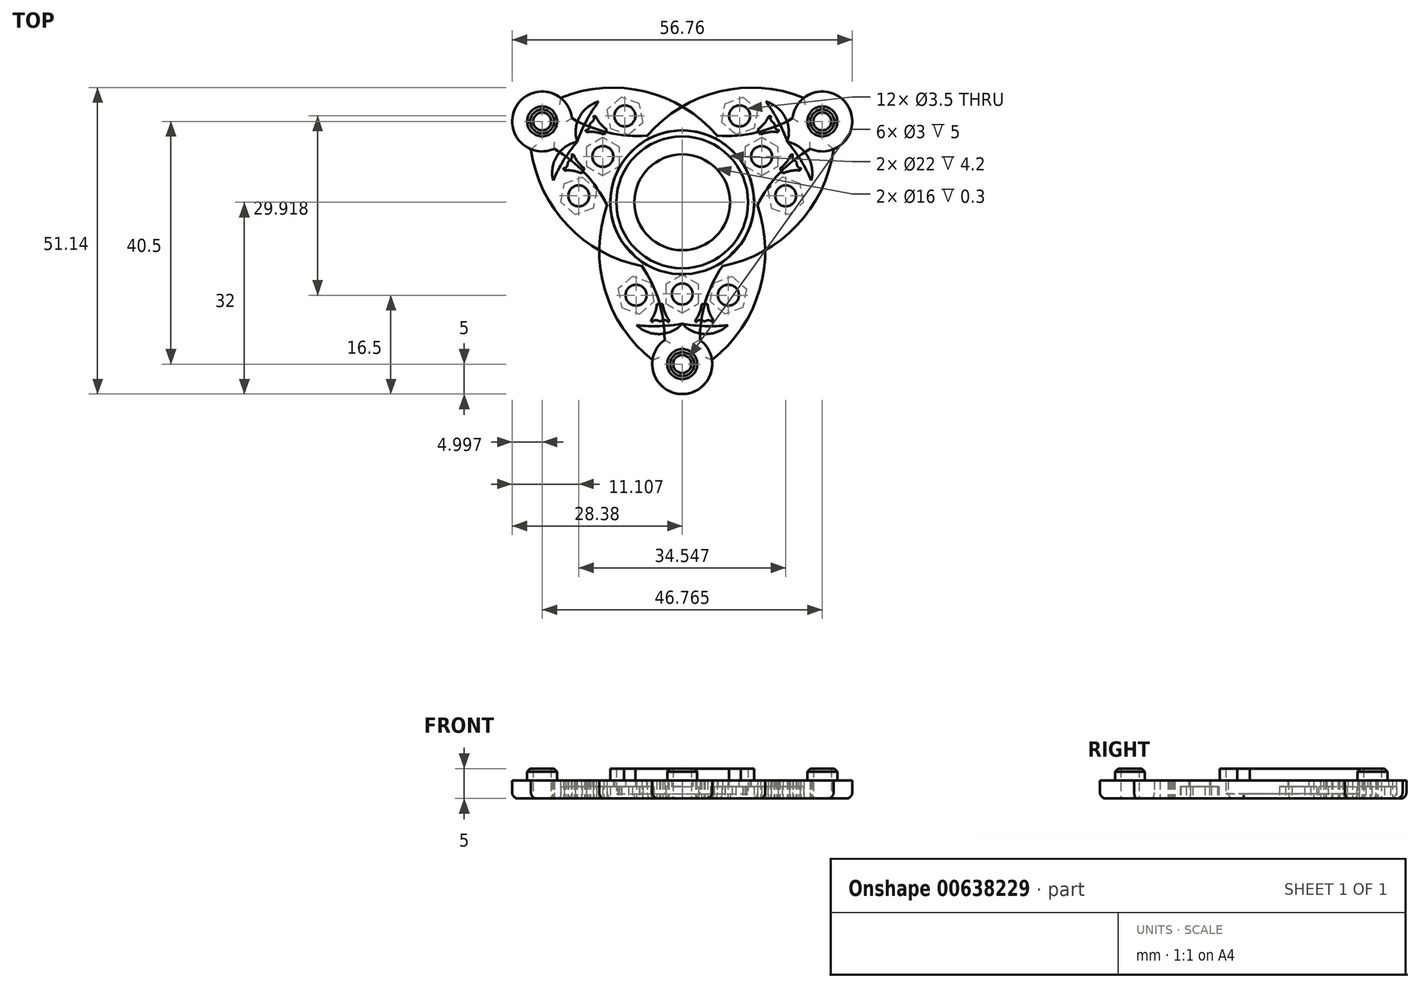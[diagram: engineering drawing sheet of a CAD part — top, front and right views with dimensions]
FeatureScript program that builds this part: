
annotation { "Feature Type Name" : "Feature", "Feature Type Description" : "" }
export const myFeature = defineFeature(function(context is Context, id is Id, definition is map)
    precondition{}
    {
        {
            var Q0;
            Q0=qCreatedBy(makeId("Top.planeOp"),FACE);
            var sketch = newSketch(context, id + "F0", { "sketchPlane" : qUnion([Q0])});
            skCircle(sketch, "E0", {"center": v(0, 0) * mm, "radius": 12 * mm});
            skArc(sketch, "E1", {"start": v(4, -27) * mm, "mid": v(12.97, -14.42) * mm, "end": v(11.96, 1) * mm});
            skCircle(sketch, "E2", {"center": v(0, -27) * mm, "radius": 4 * mm});
            skCircle(sketch, "E3", {"center": v(7.7, -15.5) * mm, "radius": 1.75 * mm});
            skArc(sketch, "E4", {"start": v(-3, -24.35) * mm, "mid": v(-4.45, -14.93) * mm, "end": v(-9.75, -7) * mm});
            skCircle(sketch, "E5.cCircle", {"center": v(7.7, -15.5) * mm, "radius": 2.75 * mm, "construction": true});
            skLineSegment(sketch, "E5.0", {"start": v(4.7, -16.54) * mm, "end": v(5.3, -13.42) * mm});
            skLineSegment(sketch, "E5.1", {"start": v(5.3, -13.42) * mm, "end": v(8.3, -12.38) * mm});
            skLineSegment(sketch, "E5.2", {"start": v(8.3, -12.38) * mm, "end": v(10.7, -14.46) * mm});
            skLineSegment(sketch, "E5.3", {"start": v(10.7, -14.46) * mm, "end": v(10.1, -17.58) * mm});
            skLineSegment(sketch, "E5.4", {"start": v(10.1, -17.58) * mm, "end": v(7.1, -18.62) * mm});
            skLineSegment(sketch, "E5.5", {"start": v(7.1, -18.62) * mm, "end": v(4.7, -16.54) * mm});
            skPoint(sketch, "E5.0.midPoint", {"position": v(5, -14.98) * mm});
            skCircle(sketch, "E6", {"center": v(0, -27) * mm, "radius": 5 * mm});
            skCircle(sketch, "E7.cCircle", {"center": v(0, -15.3) * mm, "radius": 2.75 * mm, "construction": true});
            skLineSegment(sketch, "E7.0", {"start": v(2.75, -13.71) * mm, "end": v(2.75, -16.89) * mm});
            skLineSegment(sketch, "E7.1", {"start": v(2.75, -16.89) * mm, "end": v(0, -18.48) * mm});
            skLineSegment(sketch, "E7.2", {"start": v(0, -18.48) * mm, "end": v(-2.75, -16.89) * mm});
            skLineSegment(sketch, "E7.3", {"start": v(-2.75, -16.89) * mm, "end": v(-2.75, -13.71) * mm});
            skLineSegment(sketch, "E7.4", {"start": v(-2.75, -13.71) * mm, "end": v(0, -12.12) * mm});
            skLineSegment(sketch, "E7.5", {"start": v(0, -12.12) * mm, "end": v(2.75, -13.71) * mm});
            skPoint(sketch, "E7.0.midPoint", {"position": v(2.75, -15.3) * mm});
            skCircle(sketch, "E8", {"center": v(0, -15.3) * mm, "radius": 1.75 * mm});
            skArc(sketch, "E9", {"start": v(0, -20.25) * mm, "mid": v(3.75, -21.98) * mm, "end": v(7.6, -20.5) * mm});
            skArc(sketch, "E10", {"start": v(0, -20.25) * mm, "mid": v(3.8, -20.65) * mm, "end": v(7.6, -20.5) * mm});
            skArc(sketch, "E11", {"start": v(4.9, -20) * mm, "mid": v(5.16, -19.81) * mm, "end": v(5.1, -19.5) * mm});
            skArc(sketch, "E12", {"start": v(3.6, -19.88) * mm, "mid": v(3, -19.66) * mm, "end": v(2.4, -19.88) * mm});
            skArc(sketch, "E13", {"start": v(2.3, -19.5) * mm, "mid": v(2.2, -19.78) * mm, "end": v(2.4, -20) * mm});
            skLineSegment(sketch, "E14", {"start": v(4.9, -20) * mm, "end": v(5, -19.92) * mm});
            skLineSegment(sketch, "E15", {"start": v(3.8, -19.88) * mm, "end": v(3.6, -19.88) * mm});
            skLineSegment(sketch, "E16", {"start": v(2.4, -19.88) * mm, "end": v(2.4, -20) * mm});
            skArc(sketch, "E17", {"start": v(4.25, -17) * mm, "mid": v(4.5, -18.3) * mm, "end": v(5.1, -19.5) * mm});
            skArc(sketch, "E18", {"start": v(5, -19.92) * mm, "mid": v(4.4, -19.68) * mm, "end": v(3.8, -19.88) * mm});
            skArc(sketch, "E19", {"start": v(2.3, -19.5) * mm, "mid": v(2.95, -18.31) * mm, "end": v(3.25, -17) * mm});
            skLineSegment(sketch, "E20", {"start": v(3.25, -17) * mm, "end": v(4.25, -17) * mm});
            skCircle(sketch, "E21", {"center": v(0, -27) * mm, "radius": 2.5 * mm});
            skCircle(sketch, "E22", {"center": v(0, -27) * mm, "radius": 1.5 * mm});
            skCircle(sketch, "E23", {"center": v(0, 0) * mm, "radius": 11 * mm});
            skCircle(sketch, "E24", {"center": v(0, 0) * mm, "radius": 8 * mm});
            skSolve(sketch);
        }
        {
            var Q0;
            {var subQ2=sQuery(id+"F0.wireOp",EDGE,"aa2ff135-aea7-4953-97f4-e412ee23423b.2.4");Q0=makeQuery(id+"F0.imprint","IMPRINT",FACE,{"disambiguationData":[TD([[makeQuery(id+"F0.imprint","IMPRINT",EDGE,{"derivedFrom":subQ2}),-1.0]])]});}
            var Q1;
            {var subQ8=sQuery(id+"F0.wireOp",EDGE,"aa2ff135-aea7-4953-97f4-e412ee23423b.1.4");Q1=makeQuery(id+"F0.imprint","IMPRINT",FACE,{"disambiguationData":[TD([[makeQuery(id+"F0.imprint","IMPRINT",EDGE,{"derivedFrom":subQ8}),-1.0]])]});}
            var Q2;
            {var subQ25=sQuery(id+"F0.wireOp",EDGE,"OuvVGkWf-tbSn-ko2d-VdRC-dNZ10hL7c7yv");Q2=makeQuery(id+"F0.imprint","IMPRINT",FACE,{"disambiguationData":[TD([[makeQuery(id+"F0.imprint","IMPRINT",EDGE,{"derivedFrom":subQ25}),-1.0]])]});}
            var Q3;
            {var subQ0=sQuery(id+"F0.wireOp",EDGE,"E1");var subQ1=sQuery(id+"F0.wireOp",EDGE,"E0");var subQ2=makeQuery(id+"F0.imprint","INTERSECT",VERTEX,{"derivedFrom":[subQ1,subQ0]});Q3=makeQuery(id+"F0.imprint","IMPRINT",FACE,{"disambiguationData":[TD([[makeQuery(id+"F0.imprint","IMPRINT",EDGE,{"disambiguationData":[TD([[subQ2,1.0]])],"derivedFrom":subQ1}),-1.0]])]});}
            var Q4;
            Q4=makeQuery(id+"F0.imprint","IMPRINT",FACE,{"disambiguationData":[TD([[makeQuery(id+"F0.imprint","IMPRINT",EDGE,{"derivedFrom":sQuery(id+"F0.wireOp",EDGE,"VsIOrWzV-Qm02-VE6o-2Dnz-qWALikvy4E2U")}),-1.0]])]});
            var Q5;
            {var subQ0=sQuery(id+"F0.wireOp",EDGE,"aa2ff135-aea7-4953-97f4-e412ee23423b.2.3");var subQ1=sQuery(id+"F0.wireOp",EDGE,"E0");var subQ2=makeQuery(id+"F0.imprint","INTERSECT",VERTEX,{"derivedFrom":[subQ1,subQ0]});Q5=makeQuery(id+"F0.imprint","IMPRINT",FACE,{"disambiguationData":[TD([[makeQuery(id+"F0.imprint","IMPRINT",EDGE,{"disambiguationData":[TD([[subQ2,1.0]])],"derivedFrom":subQ1}),-1.0]])]});}
            var Q6;
            {var subQ0=sQuery(id+"F0.wireOp",EDGE,"aa2ff135-aea7-4953-97f4-e412ee23423b.1.3");var subQ1=sQuery(id+"F0.wireOp",EDGE,"E0");var subQ2=makeQuery(id+"F0.imprint","INTERSECT",VERTEX,{"derivedFrom":[subQ1,subQ0]});Q6=makeQuery(id+"F0.imprint","IMPRINT",FACE,{"disambiguationData":[TD([[makeQuery(id+"F0.imprint","IMPRINT",EDGE,{"disambiguationData":[TD([[subQ2,1.0]])],"derivedFrom":subQ1}),-1.0]])]});}
            var Q7;
            {var subQ0=sQuery(id+"F0.wireOp",EDGE,"E2");var subQ1=sQuery(id+"F0.wireOp",EDGE,"E1");var subQ2=makeQuery(id+"F0.imprint","INTERSECT",VERTEX,{"derivedFrom":[subQ1,subQ0]});Q7=makeQuery(id+"F0.imprint","IMPRINT",FACE,{"disambiguationData":[TD([[makeQuery(id+"F0.imprint","IMPRINT",EDGE,{"disambiguationData":[TD([[subQ2,-1.0]])],"derivedFrom":subQ1}),-1.0]])]});}
            var Q8;
            {var subQ0=sQuery(id+"F0.wireOp",EDGE,"E2");var subQ1=sQuery(id+"F0.wireOp",EDGE,"E1");var subQ2=makeQuery(id+"F0.imprint","INTERSECT",VERTEX,{"derivedFrom":[subQ1,subQ0]});Q8=makeQuery(id+"F0.imprint","IMPRINT",FACE,{"disambiguationData":[TD([[makeQuery(id+"F0.imprint","IMPRINT",EDGE,{"disambiguationData":[TD([[subQ2,-1.0]])],"derivedFrom":subQ1}),1.0]])]});}
            var Q9;
            {var subQ0=sQuery(id+"F0.wireOp",EDGE,"aa2ff135-aea7-4953-97f4-e412ee23423b.1.1");var subQ1=sQuery(id+"F0.wireOp",EDGE,"aa2ff135-aea7-4953-97f4-e412ee23423b.1.0");var subQ2=makeQuery(id+"F0.imprint","INTERSECT",VERTEX,{"derivedFrom":[subQ1,subQ0]});Q9=makeQuery(id+"F0.imprint","IMPRINT",FACE,{"disambiguationData":[TD([[makeQuery(id+"F0.imprint","IMPRINT",EDGE,{"disambiguationData":[TD([[subQ2,-1.0]])],"derivedFrom":subQ1}),1.0]])]});}
            var Q10;
            {var subQ0=sQuery(id+"F0.wireOp",EDGE,"aa2ff135-aea7-4953-97f4-e412ee23423b.1.1");var subQ1=sQuery(id+"F0.wireOp",EDGE,"aa2ff135-aea7-4953-97f4-e412ee23423b.1.0");var subQ2=makeQuery(id+"F0.imprint","INTERSECT",VERTEX,{"derivedFrom":[subQ1,subQ0]});Q10=makeQuery(id+"F0.imprint","IMPRINT",FACE,{"disambiguationData":[TD([[makeQuery(id+"F0.imprint","IMPRINT",EDGE,{"disambiguationData":[TD([[subQ2,-1.0]])],"derivedFrom":subQ1}),-1.0]])]});}
            var Q11;
            {var subQ0=sQuery(id+"F0.wireOp",EDGE,"aa2ff135-aea7-4953-97f4-e412ee23423b.2.1");var subQ1=sQuery(id+"F0.wireOp",EDGE,"aa2ff135-aea7-4953-97f4-e412ee23423b.2.0");var subQ2=makeQuery(id+"F0.imprint","INTERSECT",VERTEX,{"derivedFrom":[subQ1,subQ0]});Q11=makeQuery(id+"F0.imprint","IMPRINT",FACE,{"disambiguationData":[TD([[makeQuery(id+"F0.imprint","IMPRINT",EDGE,{"disambiguationData":[TD([[subQ2,-1.0]])],"derivedFrom":subQ1}),-1.0]])]});}
            var Q12;
            {var subQ0=sQuery(id+"F0.wireOp",EDGE,"aa2ff135-aea7-4953-97f4-e412ee23423b.2.1");var subQ1=sQuery(id+"F0.wireOp",EDGE,"aa2ff135-aea7-4953-97f4-e412ee23423b.2.0");var subQ2=makeQuery(id+"F0.imprint","INTERSECT",VERTEX,{"derivedFrom":[subQ1,subQ0]});Q12=makeQuery(id+"F0.imprint","IMPRINT",FACE,{"disambiguationData":[TD([[makeQuery(id+"F0.imprint","IMPRINT",EDGE,{"disambiguationData":[TD([[subQ2,-1.0]])],"derivedFrom":subQ1}),1.0]])]});}
            var Q13;
            Q13=makeQuery(id+"F0.imprint","IMPRINT",FACE,{"disambiguationData":[TD([[makeQuery(id+"F0.imprint","IMPRINT",EDGE,{"derivedFrom":sQuery(id+"F0.wireOp",EDGE,"6bfdc183-4725-41ac-8b83-88aba1c862e5.2.5")}),1.0]])]});
            var Q14;
            Q14=makeQuery(id+"F0.imprint","IMPRINT",FACE,{"disambiguationData":[TD([[makeQuery(id+"F0.imprint","IMPRINT",EDGE,{"derivedFrom":sQuery(id+"F0.wireOp",EDGE,"6bfdc183-4725-41ac-8b83-88aba1c862e5.1.5")}),1.0]])]});
            var Q15;
            Q15=makeQuery(id+"F0.imprint","IMPRINT",FACE,{"disambiguationData":[TD([[makeQuery(id+"F0.imprint","IMPRINT",EDGE,{"derivedFrom":sQuery(id+"F0.wireOp",EDGE,"E5.0")}),1.0]])]});
            var Q16;
            {var subQ0=sQuery(id+"F0.wireOp",EDGE,"6bfdc183-4725-41ac-8b83-88aba1c862e5.1.3");var subQ1=sQuery(id+"F0.wireOp",EDGE,"6bfdc183-4725-41ac-8b83-88aba1c862e5.1.0");var subQ2=makeQuery(id+"F0.imprint","INTERSECT",VERTEX,{"derivedFrom":[subQ1,subQ0]});Q16=makeQuery(id+"F0.imprint","IMPRINT",FACE,{"disambiguationData":[TD([[makeQuery(id+"F0.imprint","IMPRINT",EDGE,{"disambiguationData":[TD([[subQ2,-1.0]])],"derivedFrom":subQ1}),-1.0]])]});}
            var Q17;
            {var subQ0=sQuery(id+"F0.wireOp",EDGE,"6bfdc183-4725-41ac-8b83-88aba1c862e5.2.3");var subQ1=sQuery(id+"F0.wireOp",EDGE,"6bfdc183-4725-41ac-8b83-88aba1c862e5.2.0");var subQ2=makeQuery(id+"F0.imprint","INTERSECT",VERTEX,{"derivedFrom":[subQ1,subQ0]});Q17=makeQuery(id+"F0.imprint","IMPRINT",FACE,{"disambiguationData":[TD([[makeQuery(id+"F0.imprint","IMPRINT",EDGE,{"disambiguationData":[TD([[subQ2,-1.0]])],"derivedFrom":subQ1}),-1.0]])]});}
            var Q18;
            {var subQ0=sQuery(id+"F0.wireOp",EDGE,"6bfdc183-4725-41ac-8b83-88aba1c862e5.2.3");var subQ1=sQuery(id+"F0.wireOp",EDGE,"6bfdc183-4725-41ac-8b83-88aba1c862e5.2.0");var subQ2=makeQuery(id+"F0.imprint","INTERSECT",VERTEX,{"derivedFrom":[subQ1,subQ0]});Q18=makeQuery(id+"F0.imprint","IMPRINT",FACE,{"disambiguationData":[TD([[makeQuery(id+"F0.imprint","IMPRINT",EDGE,{"disambiguationData":[TD([[subQ2,-1.0]])],"derivedFrom":subQ1}),1.0]])]});}
            var Q19;
            {var subQ0=sQuery(id+"F0.wireOp",EDGE,"6bfdc183-4725-41ac-8b83-88aba1c862e5.1.3");var subQ1=sQuery(id+"F0.wireOp",EDGE,"6bfdc183-4725-41ac-8b83-88aba1c862e5.1.0");var subQ2=makeQuery(id+"F0.imprint","INTERSECT",VERTEX,{"derivedFrom":[subQ1,subQ0]});Q19=makeQuery(id+"F0.imprint","IMPRINT",FACE,{"disambiguationData":[TD([[makeQuery(id+"F0.imprint","IMPRINT",EDGE,{"disambiguationData":[TD([[subQ2,-1.0]])],"derivedFrom":subQ1}),1.0]])]});}
            var Q20;
            Q20=makeQuery(id+"F0.imprint","IMPRINT",FACE,{"disambiguationData":[TD([[makeQuery(id+"F0.imprint","IMPRINT",EDGE,{"derivedFrom":sQuery(id+"F0.wireOp",EDGE,"E21")}),1.0]])]});
            var Q21;
            Q21=makeQuery(id+"F0.imprint","IMPRINT",FACE,{"disambiguationData":[TD([[makeQuery(id+"F0.imprint","IMPRINT",EDGE,{"derivedFrom":sQuery(id+"F0.wireOp",EDGE,"E21")}),-1.0]])]});
            var Q22;
            Q22=makeQuery(id+"F0.imprint","IMPRINT",FACE,{"disambiguationData":[TD([[makeQuery(id+"F0.imprint","IMPRINT",EDGE,{"derivedFrom":sQuery(id+"F0.wireOp",EDGE,"DYBCsW8S-FpRx-jUvW-2zEf-UEgbFwTiDSSr")}),-1.0]])]});
            var Q23;
            Q23=makeQuery(id+"F0.imprint","IMPRINT",FACE,{"disambiguationData":[TD([[makeQuery(id+"F0.imprint","IMPRINT",EDGE,{"derivedFrom":sQuery(id+"F0.wireOp",EDGE,"E23")}),-1.0]])]});
            extrude(context, id + "F1", {"entities" : qUnion([Q0, Q1, Q2, Q3, Q4, Q5, Q6, Q7, Q8, Q9, Q10, Q11, Q12, Q13, Q14, Q15, Q16, Q17, Q18, Q19, Q20, Q21, Q22, Q23]), "depth" : 3 * mm, "offsetDistance" : 25 * mm});
        }
        {
            var Q0;
            Q0=makeQuery(id+"F0.imprint","IMPRINT",FACE,{"disambiguationData":[TD([[makeQuery(id+"F0.imprint","IMPRINT",EDGE,{"derivedFrom":sQuery(id+"F0.wireOp",EDGE,"aa2ff135-aea7-4953-97f4-e412ee23423b.2.2")}),-1.0]])]});
            var Q1;
            Q1=makeQuery(id+"F0.imprint","IMPRINT",FACE,{"disambiguationData":[TD([[makeQuery(id+"F0.imprint","IMPRINT",EDGE,{"derivedFrom":sQuery(id+"F0.wireOp",EDGE,"9QQcIPAL-lVwb-CXQB-J3Kq-EtpuTVXcOksd")}),-1.0]])]});
            var Q2;
            Q2=makeQuery(id+"F0.imprint","IMPRINT",FACE,{"disambiguationData":[TD([[makeQuery(id+"F0.imprint","IMPRINT",EDGE,{"derivedFrom":sQuery(id+"F0.wireOp",EDGE,"aa2ff135-aea7-4953-97f4-e412ee23423b.1.2")}),-1.0]])]});
            var Q3;
            Q3=makeQuery(id+"F0.imprint","IMPRINT",FACE,{"disambiguationData":[TD([[makeQuery(id+"F0.imprint","IMPRINT",EDGE,{"derivedFrom":sQuery(id+"F0.wireOp",EDGE,"6bfdc183-4725-41ac-8b83-88aba1c862e5.2.4")}),-1.0]])]});
            var Q4;
            Q4=makeQuery(id+"F0.imprint","IMPRINT",FACE,{"disambiguationData":[TD([[makeQuery(id+"F0.imprint","IMPRINT",EDGE,{"derivedFrom":sQuery(id+"F0.wireOp",EDGE,"6bfdc183-4725-41ac-8b83-88aba1c862e5.1.4")}),-1.0]])]});
            var Q5;
            Q5=makeQuery(id+"F0.imprint","IMPRINT",FACE,{"disambiguationData":[TD([[makeQuery(id+"F0.imprint","IMPRINT",EDGE,{"derivedFrom":sQuery(id+"F0.wireOp",EDGE,"E21")}),1.0]])]});
            extrude(context, id + "F2", {"entities" : qUnion([Q0, Q1, Q2, Q3, Q4, Q5]), "operationType" : NewBodyOperationType.ADD, "depth" : 5 * mm, "offsetDistance" : 25 * mm});
        }
        {
            var Q0;
            Q0=makeQuery(id+"F0.imprint","IMPRINT",FACE,{"disambiguationData":[TD([[makeQuery(id+"F0.imprint","IMPRINT",EDGE,{"derivedFrom":sQuery(id+"F0.wireOp",EDGE,"E3")}),-1.0]])]});
            var Q1;
            Q1=makeQuery(id+"F0.imprint","IMPRINT",FACE,{"disambiguationData":[TD([[makeQuery(id+"F0.imprint","IMPRINT",EDGE,{"derivedFrom":sQuery(id+"F0.wireOp",EDGE,"E7.0")}),-1.0]])]});
            var Q2;
            Q2=makeQuery(id+"F0.imprint","IMPRINT",FACE,{"disambiguationData":[TD([[makeQuery(id+"F0.imprint","IMPRINT",EDGE,{"derivedFrom":sQuery(id+"F0.wireOp",EDGE,"E21")}),-1.0]])]});
            extrude(context, id + "F3", {"entities" : qUnion([Q0, Q1, Q2]), "operationType" : NewBodyOperationType.ADD, "depth" : 3 * mm, "offsetDistance" : 25 * mm, "hasSecondDirection" : true, "secondDirectionOppositeDirection" : false, "secondDirectionDepth" : 2 * mm});
        }
        {
            var Q0;
            Q0=makeQuery(id+"F0.imprint","IMPRINT",FACE,{"disambiguationData":[TD([[makeQuery(id+"F0.imprint","IMPRINT",EDGE,{"derivedFrom":sQuery(id+"F0.wireOp",EDGE,"DYBCsW8S-FpRx-jUvW-2zEf-UEgbFwTiDSSr")}),1.0]])]});
            var Q1;
            Q1=makeQuery(id+"F0.imprint","IMPRINT",FACE,{"disambiguationData":[TD([[makeQuery(id+"F0.imprint","IMPRINT",EDGE,{"derivedFrom":sQuery(id+"F0.wireOp",EDGE,"E23")}),1.0]])]});
            extrude(context, id + "F4", {"entities" : qUnion([Q0, Q1]), "operationType" : NewBodyOperationType.ADD, "depth" : 0.8 * mm, "offsetDistance" : 25 * mm});
        }
        {
            var Q0;
            Q0=makeQuery(id+"F4.opExtrude","CAP_EDGE",EDGE,{"disambiguationData":[OSD([sQuery(id+"F0.wireOp",EDGE,"DYBCsW8S-FpRx-jUvW-2zEf-UEgbFwTiDSSr")])],"isStart":false});
            var Q1;
            Q1=makeQuery(id+"FHa1pUwaDLo28C4_1.opPattern","COPY",EDGE,{"derivedFrom":makeQuery(id+"F2.opExtrude","CAP_EDGE",EDGE,{"disambiguationData":[OSD([sQuery(id+"F0.wireOp",EDGE,"E21")])],"isStart":false}),"instanceName":"1"});
            var Q2;
            Q2=makeQuery(id+"F2.opExtrude","CAP_EDGE",EDGE,{"disambiguationData":[OSD([sQuery(id+"F0.wireOp",EDGE,"E21")])],"isStart":false});
            var Q3;
            Q3=makeQuery(id+"FHa1pUwaDLo28C4_1.opPattern","COPY",EDGE,{"derivedFrom":makeQuery(id+"F2.opExtrude","CAP_EDGE",EDGE,{"disambiguationData":[OSD([sQuery(id+"F0.wireOp",EDGE,"E21")])],"isStart":false}),"instanceName":"2"});
            chamfer(context, id + "F5", {"entities" : qUnion([Q0, Q1, Q2, Q3]), "width" : .5 * mm, "tangentPropagation" : true});
        }
        {
            var Q0;
            Q0=makeQuery(id+"F1.opExtrude","CAP_EDGE",EDGE,{"disambiguationData":[OSD([sQuery(id+"F0.wireOp",EDGE,"E4")])],"isStart":true});
            var Q1;
            Q1=makeQuery(id+"F1.opExtrude","CAP_EDGE",EDGE,{"disambiguationData":[OSD([sQuery(id+"F0.wireOp",EDGE,"E6")])],"isStart":true});
            var Q2;
            Q2=makeQuery(id+"F1.opExtrude","CAP_EDGE",EDGE,{"disambiguationData":[OSD([sQuery(id+"F0.wireOp",EDGE,"E1")])],"isStart":true});
            fillet(context, id + "F6", {"entities" : qUnion([Q0, Q1, Q2]), "radius" : 1 * mm, "tangentPropagation" : true, "allowEdgeOverflow" : false});
        }
        {
            var Q0;
            Q0=makeQuery(id+"F4.opExtrude","CAP_EDGE",EDGE,{"disambiguationData":[OSD([sQuery(id+"F0.wireOp",EDGE,"E24")])],"isStart":true});
            fillet(context, id + "F7", {"entities" : qUnion([Q0]), "radius" : .5 * mm, "tangentPropagation" : true, "allowEdgeOverflow" : false});
        }
        {
            var Q0;
            Q0=makeQuery(id+"F1.opExtrude","SWEPT_BODY",BODY,{"disambiguationData":[OSD([sQuery(id+"F0.wireOp",EDGE,"E0"),sQuery(id+"F0.wireOp",EDGE,"E1"),sQuery(id+"F0.wireOp",EDGE,"E4"),sQuery(id+"F0.wireOp",EDGE,"E5.0"),sQuery(id+"F0.wireOp",EDGE,"E5.1"),sQuery(id+"F0.wireOp",EDGE,"E5.2"),sQuery(id+"F0.wireOp",EDGE,"E5.3"),sQuery(id+"F0.wireOp",EDGE,"E5.4"),sQuery(id+"F0.wireOp",EDGE,"E5.5"),sQuery(id+"F0.wireOp",EDGE,"E6"),sQuery(id+"F0.wireOp",EDGE,"E7.0"),sQuery(id+"F0.wireOp",EDGE,"E7.1"),sQuery(id+"F0.wireOp",EDGE,"E7.2"),sQuery(id+"F0.wireOp",EDGE,"E7.3"),sQuery(id+"F0.wireOp",EDGE,"E7.4"),sQuery(id+"F0.wireOp",EDGE,"E7.5"),sQuery(id+"F0.wireOp",EDGE,"E9"),sQuery(id+"F0.wireOp",EDGE,"E10"),sQuery(id+"F0.wireOp",EDGE,"E11"),sQuery(id+"F0.wireOp",EDGE,"E12"),sQuery(id+"F0.wireOp",EDGE,"E13"),sQuery(id+"F0.wireOp",EDGE,"E14"),sQuery(id+"F0.wireOp",EDGE,"E15"),sQuery(id+"F0.wireOp",EDGE,"E16"),sQuery(id+"F0.wireOp",EDGE,"E17"),sQuery(id+"F0.wireOp",EDGE,"E18"),sQuery(id+"F0.wireOp",EDGE,"E19"),sQuery(id+"F0.wireOp",EDGE,"E20"),sQuery(id+"F0.wireOp",EDGE,"E22"),sQuery(id+"F0.wireOp",EDGE,"E23")])]});
            var Q1;
            Q1=sQuery(id+"F0.wireOp",EDGE,"E23");
            circularPattern(context, id + "F8", {"operationType" : NewBodyOperationType.ADD, "entities" : qUnion([Q0]), "axis" : qUnion([Q1]), "angle" : 360 * degree, "instanceCount" : 3, "equalSpace" : true});
        }
        {
            var Q0;
            Q0=makeQuery(id+"F0.imprint","IMPRINT",FACE,{"disambiguationData":[TD([[makeQuery(id+"F0.imprint","IMPRINT",EDGE,{"derivedFrom":sQuery(id+"F0.wireOp",EDGE,"E23")}),-1.0]])]});
            extrude(context, id + "F9", {"entities" : qUnion([Q0]), "operationType" : NewBodyOperationType.ADD, "depth" : 5 * mm, "offsetDistance" : 25 * mm});
        }
        {
            var Q0;
            Q0=makeQuery(id+"F8.opPattern","COPY",BODY,{"derivedFrom":makeQuery(id+"F1.opExtrude","SWEPT_BODY",BODY,{"disambiguationData":[OSD([sQuery(id+"F0.wireOp",EDGE,"E0"),sQuery(id+"F0.wireOp",EDGE,"E1"),sQuery(id+"F0.wireOp",EDGE,"E4"),sQuery(id+"F0.wireOp",EDGE,"E5.0"),sQuery(id+"F0.wireOp",EDGE,"E5.1"),sQuery(id+"F0.wireOp",EDGE,"E5.2"),sQuery(id+"F0.wireOp",EDGE,"E5.3"),sQuery(id+"F0.wireOp",EDGE,"E5.4"),sQuery(id+"F0.wireOp",EDGE,"E5.5"),sQuery(id+"F0.wireOp",EDGE,"E6"),sQuery(id+"F0.wireOp",EDGE,"E7.0"),sQuery(id+"F0.wireOp",EDGE,"E7.1"),sQuery(id+"F0.wireOp",EDGE,"E7.2"),sQuery(id+"F0.wireOp",EDGE,"E7.3"),sQuery(id+"F0.wireOp",EDGE,"E7.4"),sQuery(id+"F0.wireOp",EDGE,"E7.5"),sQuery(id+"F0.wireOp",EDGE,"E9"),sQuery(id+"F0.wireOp",EDGE,"E10"),sQuery(id+"F0.wireOp",EDGE,"E11"),sQuery(id+"F0.wireOp",EDGE,"E12"),sQuery(id+"F0.wireOp",EDGE,"E13"),sQuery(id+"F0.wireOp",EDGE,"E14"),sQuery(id+"F0.wireOp",EDGE,"E15"),sQuery(id+"F0.wireOp",EDGE,"E16"),sQuery(id+"F0.wireOp",EDGE,"E17"),sQuery(id+"F0.wireOp",EDGE,"E18"),sQuery(id+"F0.wireOp",EDGE,"E19"),sQuery(id+"F0.wireOp",EDGE,"E20"),sQuery(id+"F0.wireOp",EDGE,"E22"),sQuery(id+"F0.wireOp",EDGE,"E23")])]}),"instanceName":"2"});
            var Q1;
            Q1=makeQuery(id+"F1.opExtrude","SWEPT_BODY",BODY,{"disambiguationData":[OSD([sQuery(id+"F0.wireOp",EDGE,"E0"),sQuery(id+"F0.wireOp",EDGE,"E1"),sQuery(id+"F0.wireOp",EDGE,"E4"),sQuery(id+"F0.wireOp",EDGE,"E5.0"),sQuery(id+"F0.wireOp",EDGE,"E5.1"),sQuery(id+"F0.wireOp",EDGE,"E5.2"),sQuery(id+"F0.wireOp",EDGE,"E5.3"),sQuery(id+"F0.wireOp",EDGE,"E5.4"),sQuery(id+"F0.wireOp",EDGE,"E5.5"),sQuery(id+"F0.wireOp",EDGE,"E6"),sQuery(id+"F0.wireOp",EDGE,"E7.0"),sQuery(id+"F0.wireOp",EDGE,"E7.1"),sQuery(id+"F0.wireOp",EDGE,"E7.2"),sQuery(id+"F0.wireOp",EDGE,"E7.3"),sQuery(id+"F0.wireOp",EDGE,"E7.4"),sQuery(id+"F0.wireOp",EDGE,"E7.5"),sQuery(id+"F0.wireOp",EDGE,"E9"),sQuery(id+"F0.wireOp",EDGE,"E10"),sQuery(id+"F0.wireOp",EDGE,"E11"),sQuery(id+"F0.wireOp",EDGE,"E12"),sQuery(id+"F0.wireOp",EDGE,"E13"),sQuery(id+"F0.wireOp",EDGE,"E14"),sQuery(id+"F0.wireOp",EDGE,"E15"),sQuery(id+"F0.wireOp",EDGE,"E16"),sQuery(id+"F0.wireOp",EDGE,"E17"),sQuery(id+"F0.wireOp",EDGE,"E18"),sQuery(id+"F0.wireOp",EDGE,"E19"),sQuery(id+"F0.wireOp",EDGE,"E20"),sQuery(id+"F0.wireOp",EDGE,"E22"),sQuery(id+"F0.wireOp",EDGE,"E23")])]});
            var Q2;
            Q2=makeQuery(id+"F8.opPattern","COPY",BODY,{"derivedFrom":makeQuery(id+"F1.opExtrude","SWEPT_BODY",BODY,{"disambiguationData":[OSD([sQuery(id+"F0.wireOp",EDGE,"E0"),sQuery(id+"F0.wireOp",EDGE,"E1"),sQuery(id+"F0.wireOp",EDGE,"E4"),sQuery(id+"F0.wireOp",EDGE,"E5.0"),sQuery(id+"F0.wireOp",EDGE,"E5.1"),sQuery(id+"F0.wireOp",EDGE,"E5.2"),sQuery(id+"F0.wireOp",EDGE,"E5.3"),sQuery(id+"F0.wireOp",EDGE,"E5.4"),sQuery(id+"F0.wireOp",EDGE,"E5.5"),sQuery(id+"F0.wireOp",EDGE,"E6"),sQuery(id+"F0.wireOp",EDGE,"E7.0"),sQuery(id+"F0.wireOp",EDGE,"E7.1"),sQuery(id+"F0.wireOp",EDGE,"E7.2"),sQuery(id+"F0.wireOp",EDGE,"E7.3"),sQuery(id+"F0.wireOp",EDGE,"E7.4"),sQuery(id+"F0.wireOp",EDGE,"E7.5"),sQuery(id+"F0.wireOp",EDGE,"E9"),sQuery(id+"F0.wireOp",EDGE,"E10"),sQuery(id+"F0.wireOp",EDGE,"E11"),sQuery(id+"F0.wireOp",EDGE,"E12"),sQuery(id+"F0.wireOp",EDGE,"E13"),sQuery(id+"F0.wireOp",EDGE,"E14"),sQuery(id+"F0.wireOp",EDGE,"E15"),sQuery(id+"F0.wireOp",EDGE,"E16"),sQuery(id+"F0.wireOp",EDGE,"E17"),sQuery(id+"F0.wireOp",EDGE,"E18"),sQuery(id+"F0.wireOp",EDGE,"E19"),sQuery(id+"F0.wireOp",EDGE,"E20"),sQuery(id+"F0.wireOp",EDGE,"E22"),sQuery(id+"F0.wireOp",EDGE,"E23")])]}),"instanceName":"1"});
            var Q3;
            Q3=qCreatedBy(makeId("Right.planeOp"),FACE);
            mirror(context, id + "F10", {"entities" : qUnion([Q0, Q1, Q2]), "mirrorPlane" : qUnion([Q3])});
        }
    });
